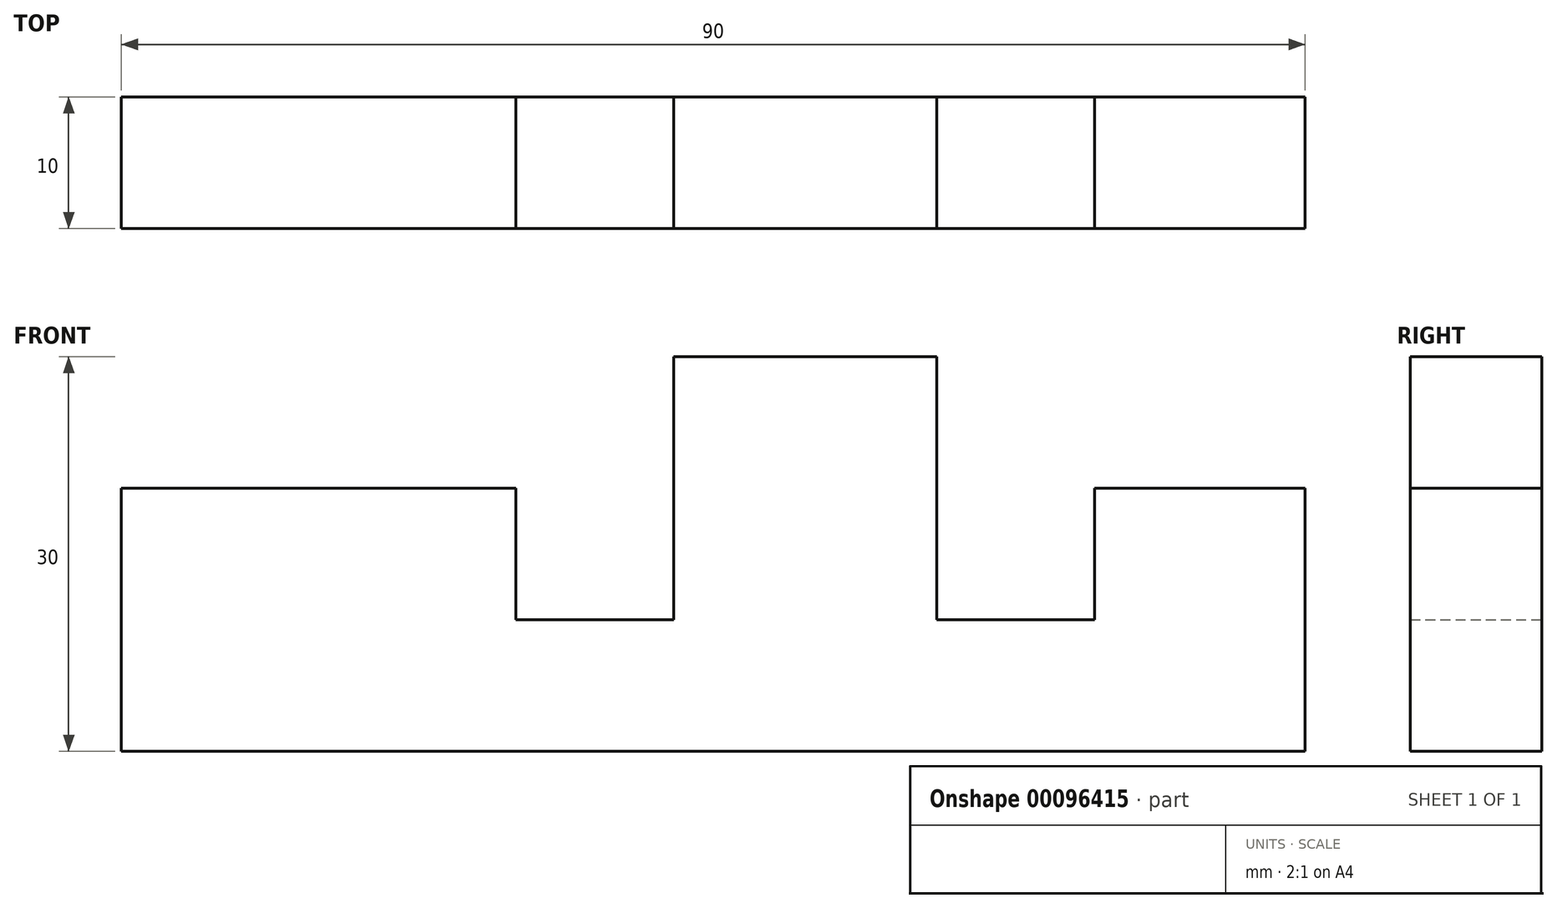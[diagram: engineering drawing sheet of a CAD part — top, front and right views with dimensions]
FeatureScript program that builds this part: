
annotation { "Feature Type Name" : "Feature", "Feature Type Description" : "" }
export const myFeature = defineFeature(function(context is Context, id is Id, definition is map)
    precondition{}
    {
        {
            var Q0;
            Q0=qCreatedBy(makeId("Front.planeOp"),FACE);
            var sketch = newSketch(context, id + "F0", { "sketchPlane" : qUnion([Q0])});
            skLineSegment(sketch, "E0", {"start": v(0, 0) * mm, "end": v(90, 0) * mm});
            skLineSegment(sketch, "E1", {"start": v(90, 0) * mm, "end": v(90, 20) * mm});
            skLineSegment(sketch, "E2", {"start": v(90, 20) * mm, "end": v(74, 20) * mm});
            skLineSegment(sketch, "E3", {"start": v(74, 20) * mm, "end": v(74, 10) * mm});
            skLineSegment(sketch, "E4", {"start": v(74, 10) * mm, "end": v(62, 10) * mm});
            skLineSegment(sketch, "E5", {"start": v(62, 10) * mm, "end": v(62, 30) * mm});
            skLineSegment(sketch, "E6", {"start": v(62, 30) * mm, "end": v(42, 30) * mm});
            skLineSegment(sketch, "E7", {"start": v(42, 30) * mm, "end": v(42, 10) * mm});
            skLineSegment(sketch, "E8", {"start": v(42, 10) * mm, "end": v(30, 10) * mm});
            skLineSegment(sketch, "E9", {"start": v(30, 10) * mm, "end": v(30, 20) * mm});
            skLineSegment(sketch, "E10", {"start": v(30, 20) * mm, "end": v(0, 20) * mm});
            skLineSegment(sketch, "E11", {"start": v(0, 20) * mm, "end": v(0, 0) * mm});
            skSolve(sketch);
        }
        {
            var Q0;
            Q0=makeQuery(id+"F0.imprint","IMPRINT",FACE,{"disambiguationData":[TD([[makeQuery(id+"F0.imprint","IMPRINT",EDGE,{"derivedFrom":sQuery(id+"F0.wireOp",EDGE,"E0")}),1.0]])]});
            var Q1;
            Q1 = qSketchRegion(id + "F0", true);
            extrude(context, id + "F1", {"entities" : qUnion([Q0, Q1]), "depth" : 10 * mm});
        }
    });
